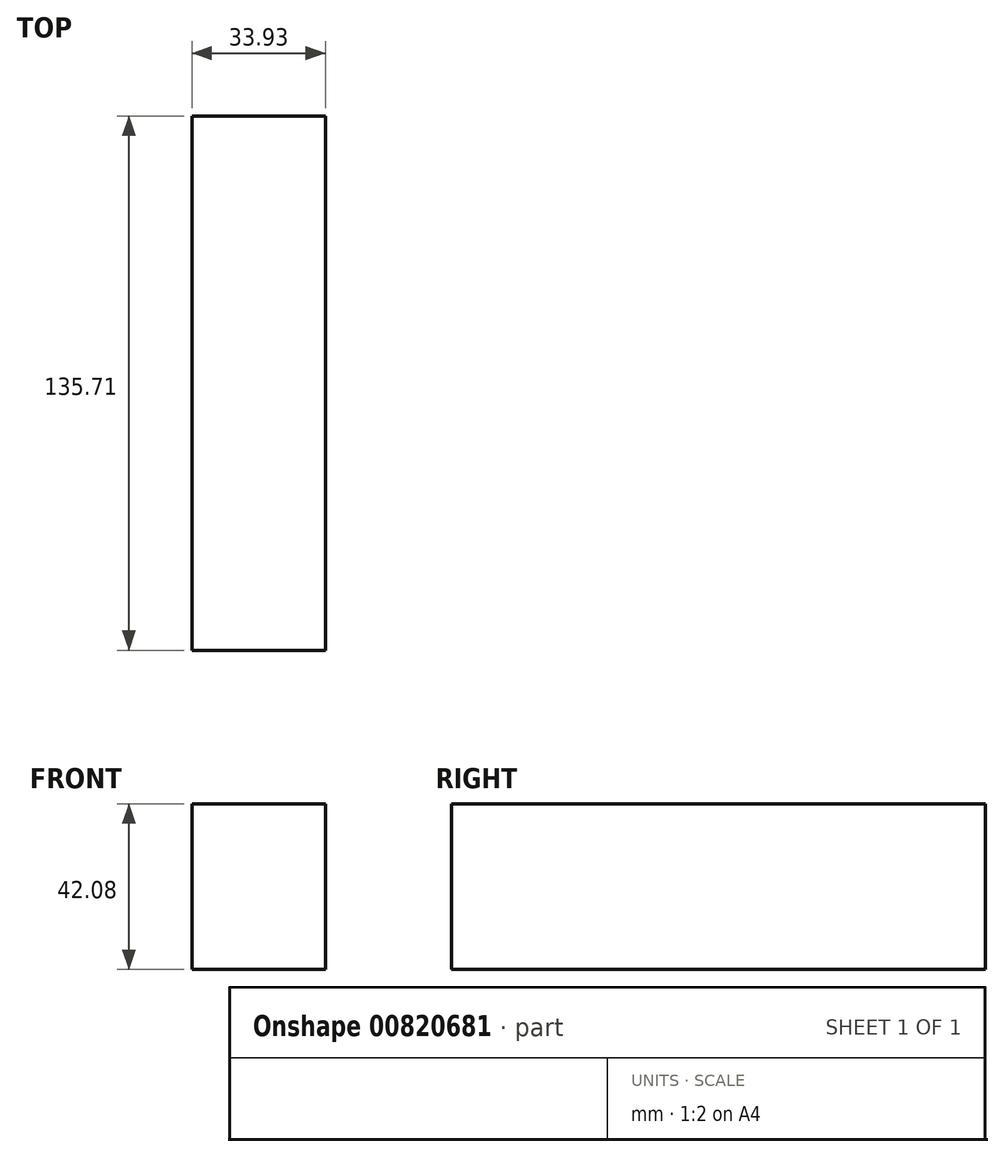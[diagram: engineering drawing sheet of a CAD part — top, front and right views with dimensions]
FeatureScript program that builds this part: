
annotation { "Feature Type Name" : "Feature", "Feature Type Description" : "" }
export const myFeature = defineFeature(function(context is Context, id is Id, definition is map)
    precondition{}
    {
        {
            var Q0;
            Q0=qCreatedBy(makeId("Front.planeOp"),FACE);
            var sketch = newSketch(context, id + "F0", { "sketchPlane" : qUnion([Q0])});
            skLineSegment(sketch, "E0.bottom", {"start": v(33.93, 42.08) * mm, "end": v(0, 42.08) * mm});
            skLineSegment(sketch, "E0.top", {"start": v(33.93, 0) * mm, "end": v(0, 0) * mm});
            skLineSegment(sketch, "E0.left", {"start": v(33.93, 42.08) * mm, "end": v(33.93, 0) * mm});
            skLineSegment(sketch, "E0.right", {"start": v(0, 42.08) * mm, "end": v(0, 0) * mm});
            skSolve(sketch);
        }
        {
            var Q0;
            Q0=makeQuery(id+"F0.imprint","IMPRINT",FACE,{"disambiguationData":[TD([[makeQuery(id+"F0.imprint","IMPRINT",EDGE,{"derivedFrom":sQuery(id+"F0.wireOp",EDGE,"E0.bottom")}),1.0]])]});
            extrude(context, id + "F1", {"entities" : qUnion([Q0]), "depth" : 135.7 * mm, "offsetDistance" : 25.4 * mm});
        }
    });
